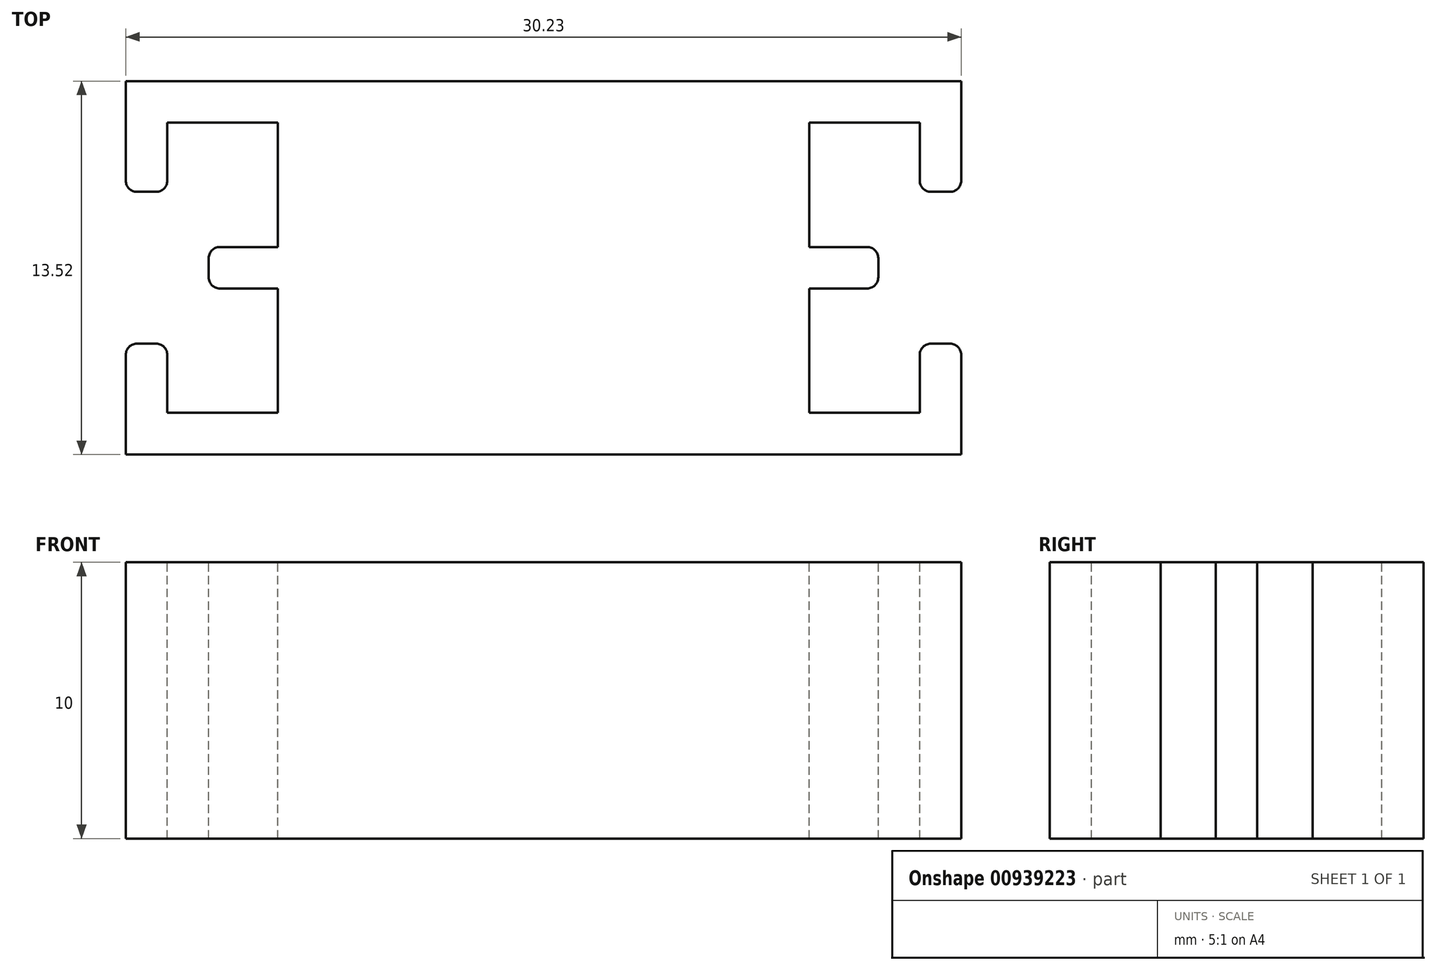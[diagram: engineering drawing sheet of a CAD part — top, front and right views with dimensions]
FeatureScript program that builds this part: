
annotation { "Feature Type Name" : "Feature", "Feature Type Description" : "" }
export const myFeature = defineFeature(function(context is Context, id is Id, definition is map)
    precondition{}
    {
        {
            var Q0;
            Q0=qCreatedBy(makeId("Front.planeOp"),FACE);
            var sketch = newSketch(context, id + "F0", { "sketchPlane" : qUnion([Q0])});
            skLineSegment(sketch, "E0", {"start": v(15.16, 6.76) * mm, "end": v(0, 6.76) * mm});
            skLineSegment(sketch, "E1", {"start": v(15.16, -6.76) * mm, "end": v(0, -6.76) * mm});
            skLineSegment(sketch, "E2", {"start": v(15.16, 6.76) * mm, "end": v(15.16, 2.75) * mm});
            skLineSegment(sketch, "E3", {"start": v(15.16, 2.75) * mm, "end": v(13.66, 2.75) * mm});
            skLineSegment(sketch, "E4", {"start": v(13.66, 2.75) * mm, "end": v(13.66, 5.25) * mm});
            skLineSegment(sketch, "E5", {"start": v(13.66, 5.25) * mm, "end": v(9.66, 5.25) * mm});
            skLineSegment(sketch, "E6", {"start": v(9.66, 5.25) * mm, "end": v(9.66, 0.75) * mm});
            skLineSegment(sketch, "E7", {"start": v(9.66, 0.75) * mm, "end": v(12.16, 0.75) * mm});
            skLineSegment(sketch, "E8", {"start": v(12.16, 0.75) * mm, "end": v(12.16, 0) * mm});
            skLineSegment(sketch, "E9", {"start": v(12.16, 0) * mm, "end": v(12.16, -0.75) * mm});
            skLineSegment(sketch, "E10", {"start": v(12.16, -0.75) * mm, "end": v(9.66, -0.75) * mm});
            skLineSegment(sketch, "E11", {"start": v(9.66, -0.75) * mm, "end": v(9.66, -5.25) * mm});
            skLineSegment(sketch, "E12", {"start": v(9.66, -5.25) * mm, "end": v(13.66, -5.25) * mm});
            skLineSegment(sketch, "E13", {"start": v(13.66, -5.25) * mm, "end": v(13.66, -2.75) * mm});
            skLineSegment(sketch, "E14", {"start": v(13.66, -2.75) * mm, "end": v(15.16, -2.75) * mm});
            skLineSegment(sketch, "E15", {"start": v(15.16, -2.75) * mm, "end": v(15.16, -6.76) * mm});
            skLineSegment(sketch, "E16", {"start": v(-15.07, -6.76) * mm, "end": v(0, -6.76) * mm});
            skLineSegment(sketch, "E17", {"start": v(-15.07, 6.76) * mm, "end": v(0, 6.76) * mm});
            skLineSegment(sketch, "E18", {"start": v(-15.07, -6.76) * mm, "end": v(-15.07, -2.75) * mm});
            skLineSegment(sketch, "E19", {"start": v(-15.07, -2.75) * mm, "end": v(-13.57, -2.75) * mm});
            skLineSegment(sketch, "E20", {"start": v(-13.57, -2.75) * mm, "end": v(-13.57, -5.25) * mm});
            skLineSegment(sketch, "E21", {"start": v(-13.57, -5.25) * mm, "end": v(-9.57, -5.25) * mm});
            skLineSegment(sketch, "E22", {"start": v(-9.57, -5.25) * mm, "end": v(-9.57, -0.75) * mm});
            skLineSegment(sketch, "E23", {"start": v(-9.57, -0.75) * mm, "end": v(-12.07, -0.75) * mm});
            skLineSegment(sketch, "E24", {"start": v(-12.07, -0.75) * mm, "end": v(-12.07, 0) * mm});
            skLineSegment(sketch, "E25", {"start": v(-12.07, 0) * mm, "end": v(-12.07, 0.75) * mm});
            skLineSegment(sketch, "E26", {"start": v(-12.07, 0.75) * mm, "end": v(-9.57, 0.75) * mm});
            skLineSegment(sketch, "E27", {"start": v(-9.57, 0.75) * mm, "end": v(-9.57, 5.25) * mm});
            skLineSegment(sketch, "E28", {"start": v(-9.57, 5.25) * mm, "end": v(-13.57, 5.25) * mm});
            skLineSegment(sketch, "E29", {"start": v(-13.57, 5.25) * mm, "end": v(-13.57, 2.75) * mm});
            skLineSegment(sketch, "E30", {"start": v(-13.57, 2.75) * mm, "end": v(-15.07, 2.75) * mm});
            skLineSegment(sketch, "E31", {"start": v(-15.07, 2.75) * mm, "end": v(-15.07, 6.76) * mm});
            skSolve(sketch);
        }
        {
            var Q0;
            Q0=makeQuery(id+"F0.imprint","IMPRINT",FACE,{"disambiguationData":[TD([[makeQuery(id+"F0.imprint","IMPRINT",EDGE,{"derivedFrom":sQuery(id+"F0.wireOp",EDGE,"E0")}),1.0]])]});
            extrude(context, id + "F1", {"entities" : qUnion([Q0]), "depth" : 10 * mm, "offsetDistance" : 25 * mm});
        }
        {
            var Q0;
            Q0=makeQuery(id+"F1.opExtrude","SWEPT_EDGE",EDGE,{"disambiguationData":[OSD([sQuery(id+"F0.wireOp",EDGE,"E2"),sQuery(id+"F0.wireOp",EDGE,"E3")])]});
            var Q1;
            Q1=makeQuery(id+"F1.opExtrude","SWEPT_EDGE",EDGE,{"disambiguationData":[OSD([sQuery(id+"F0.wireOp",EDGE,"E3"),sQuery(id+"F0.wireOp",EDGE,"E4")])]});
            var Q2;
            Q2=makeQuery(id+"F1.opExtrude","SWEPT_EDGE",EDGE,{"disambiguationData":[OSD([sQuery(id+"F0.wireOp",EDGE,"E7"),sQuery(id+"F0.wireOp",EDGE,"E8")])]});
            var Q3;
            Q3=makeQuery(id+"F1.opExtrude","SWEPT_EDGE",EDGE,{"disambiguationData":[OSD([sQuery(id+"F0.wireOp",EDGE,"E9"),sQuery(id+"F0.wireOp",EDGE,"E10")])]});
            var Q4;
            Q4=makeQuery(id+"F1.opExtrude","SWEPT_EDGE",EDGE,{"disambiguationData":[OSD([sQuery(id+"F0.wireOp",EDGE,"E14"),sQuery(id+"F0.wireOp",EDGE,"E15")])]});
            var Q5;
            Q5=makeQuery(id+"F1.opExtrude","SWEPT_EDGE",EDGE,{"disambiguationData":[OSD([sQuery(id+"F0.wireOp",EDGE,"E13"),sQuery(id+"F0.wireOp",EDGE,"E14")])]});
            var Q6;
            Q6=makeQuery(id+"F1.opExtrude","SWEPT_EDGE",EDGE,{"disambiguationData":[OSD([sQuery(id+"F0.wireOp",EDGE,"E19"),sQuery(id+"F0.wireOp",EDGE,"E20")])]});
            var Q7;
            Q7=makeQuery(id+"F1.opExtrude","SWEPT_EDGE",EDGE,{"disambiguationData":[OSD([sQuery(id+"F0.wireOp",EDGE,"E18"),sQuery(id+"F0.wireOp",EDGE,"E19")])]});
            var Q8;
            Q8=makeQuery(id+"F1.opExtrude","SWEPT_EDGE",EDGE,{"disambiguationData":[OSD([sQuery(id+"F0.wireOp",EDGE,"E25"),sQuery(id+"F0.wireOp",EDGE,"E26")])]});
            var Q9;
            Q9=makeQuery(id+"F1.opExtrude","SWEPT_EDGE",EDGE,{"disambiguationData":[OSD([sQuery(id+"F0.wireOp",EDGE,"E23"),sQuery(id+"F0.wireOp",EDGE,"E24")])]});
            var Q10;
            Q10=makeQuery(id+"F1.opExtrude","SWEPT_EDGE",EDGE,{"disambiguationData":[OSD([sQuery(id+"F0.wireOp",EDGE,"E29"),sQuery(id+"F0.wireOp",EDGE,"E30")])]});
            var Q11;
            Q11=makeQuery(id+"F1.opExtrude","SWEPT_EDGE",EDGE,{"disambiguationData":[OSD([sQuery(id+"F0.wireOp",EDGE,"E30"),sQuery(id+"F0.wireOp",EDGE,"E31")])]});
            fillet(context, id + "F2", {"entities" : qUnion([Q0, Q1, Q2, Q3, Q4, Q5, Q6, Q7, Q8, Q9, Q10, Q11]), "radius" : .4 * mm, "tangentPropagation" : true, "allowEdgeOverflow" : false});
        }
        {
            var Q0;
            Q0=makeQuery(id+"F1.opExtrude","SWEPT_BODY",BODY,{"disambiguationData":[OSD([sQuery(id+"F0.wireOp",EDGE,"E0"),sQuery(id+"F0.wireOp",EDGE,"E1"),sQuery(id+"F0.wireOp",EDGE,"E2"),sQuery(id+"F0.wireOp",EDGE,"E3"),sQuery(id+"F0.wireOp",EDGE,"E4"),sQuery(id+"F0.wireOp",EDGE,"E5"),sQuery(id+"F0.wireOp",EDGE,"E6"),sQuery(id+"F0.wireOp",EDGE,"E7"),sQuery(id+"F0.wireOp",EDGE,"E8"),sQuery(id+"F0.wireOp",EDGE,"E9"),sQuery(id+"F0.wireOp",EDGE,"E10"),sQuery(id+"F0.wireOp",EDGE,"E11"),sQuery(id+"F0.wireOp",EDGE,"E12"),sQuery(id+"F0.wireOp",EDGE,"E13"),sQuery(id+"F0.wireOp",EDGE,"E14"),sQuery(id+"F0.wireOp",EDGE,"E15"),sQuery(id+"F0.wireOp",EDGE,"E16"),sQuery(id+"F0.wireOp",EDGE,"E17"),sQuery(id+"F0.wireOp",EDGE,"E18"),sQuery(id+"F0.wireOp",EDGE,"E19"),sQuery(id+"F0.wireOp",EDGE,"E20"),sQuery(id+"F0.wireOp",EDGE,"E21"),sQuery(id+"F0.wireOp",EDGE,"E22"),sQuery(id+"F0.wireOp",EDGE,"E23"),sQuery(id+"F0.wireOp",EDGE,"E24"),sQuery(id+"F0.wireOp",EDGE,"E25"),sQuery(id+"F0.wireOp",EDGE,"E26"),sQuery(id+"F0.wireOp",EDGE,"E27"),sQuery(id+"F0.wireOp",EDGE,"E28"),sQuery(id+"F0.wireOp",EDGE,"E29"),sQuery(id+"F0.wireOp",EDGE,"E30"),sQuery(id+"F0.wireOp",EDGE,"E31")])]});
            var Q1;
            Q1=makeQuery(id+"F1.opExtrude","CAP_EDGE",EDGE,{"disambiguationData":[OSD([sQuery(id+"F0.wireOp",EDGE,"E1"),sQuery(id+"F0.wireOp",EDGE,"E16")])],"isStart":false});
            transform(context, id + "F3", {"entities" : qUnion([Q0]), "transformType" : TransformType.ROTATION, "transformAxis" : qUnion([Q1]), "angle" : 90 * degree, "makeCopy" : false});
        }
    });
